# Revit family: IS_ConnectSpace_Multiproduct_BIM_DE_E0372;E0373
name_source: partatom
category: Casework
revit_build: Autodesk Revit 2015 (Build: 20140606_1530(x64)
units: mm (PartAtom-declared; Revit-internal decimal feet)

## types (8) — shared parameters
Accessories = www.idealstandard.de\ersatzteile
AreaUnits = millimeters
Assembly Code = C1030200
AssetType = Fixed
Brand = Ideal Standard
CodePerformance = FSC, EN 14749:2005
ConnectionType = Mechanical
Default Elevation = 800 mm  [stored 2.62467 ft]
Depth = 250 mm  [stored 0.82021 ft]
DurationUnit = year
ExpectedLife = 25
Height = 500 mm
IfcExportAs = IfcFurnitureType
IfcExportType = Bathroom integrated furniture
InstallationInstructions = www.idealstandard.de\produkte
LinearUnits = millimeters
ManufacturerURL = www.idealstandard.com
Material = Varies, see product information
MetalMtl = ISI_IdealStandard_Furniture_Chrome_Render
NBSDescription = Bathroom integrated furniture
NBSReference = 45-35-72/320
NominalDepth = 250 mm  [stored 0.82021 ft]
NominalHeight = 500 mm
NominalLength = 250 mm  [stored 0.82021 ft]
ProductInformation = www.idealstandard.de/produkte
Shape = Rectangular
Space = Internal
SpareParts = www.idealstandard.de/ersatzteile
Style = Bathroom cabinets
SustainabilityPerformance = FSC
URL = www.idealstandard.com
Uniclass2015Code = Pr_40_30_78_03
Uniclass2015Title = Bathroom cabinets
Uniclass2015Version = Products v1.1
Version = 2
VolumeUnits = Litres
WarrantyDurationUnit = year
zero-valued in all types: Cost

## per-type parameters (varying)
| type | BIMObjectName | BarCode | Color | Description | Features | Finish | LaminateMtl | MainColor | Model | ModelNumber | ModelReference | Name | NettWeight | NominalWidth | Size | Width |
| E0403WG - Concept Space 300 mm - Add on - Guest Unit - Gloss White | ISI_IdealStandard_BathroomIntegratedFurniture_ConnectSpace_E0403WG | 5017830455165 | Gloss White | E0373WG CONNECT SPACE side unit 300x242mm, 1 door | CONNECT SPACE side unit 300x242mm, 1 door | Gloss White | ISI_IdealStandard_Furniture_Laminate_GlossWhite_WG_Render | Gloss White | E0373WG | E0373WG | E0373WG CONNECT SPACE side unit 300x242mm, 1 door | BathroomIntegratedFurniture_ConnectSpace_E0403WG_IdealStandard | 8.75 Kg | 300 mm | 501 x 250 x 300 mm | 300 mm |
| E0403KS - Concept Space 300 mm - Add on - Guest Unit - Elm | ISI_IdealStandard_BathroomIntegratedFurniture_ConnectSpace_E0403KS | 5017830455134 | Elm | E0373KS CONNECT SPACE side unit 300x242mm, 1 door | CONNECT SPACE side unit 300x242mm, 1 door | Elm | ISI_IdealStandard_Furniture_Laminate_Elm_KS_Render | Elm | E0373KS | E0373KS | E0373KS CONNECT SPACE side unit 300x242mm, 1 door | BathroomIntegratedFurniture_ConnectSpace_E0403KS_IdealStandard | 8.75 Kg | 300 mm | 501 x 250 x 300 mm | 300 mm |
| E0403KR - Concept Space 300 mm - Add on - Guest Unit - Dark Grey | ISI_IdealStandard_BathroomIntegratedFurniture_ConnectSpace_E0403KR | 5017830455127 | Gloss Grey | E0373KR CONNECT SPACE side unit 300x242mm, 1 door | CONNECT SPACE side unit 300x242mm, 1 door | Gloss Grey | ISI_IdealStandard_Furniture_Laminate_DarkGreyKR_Render | Gloss Grey | E0373KR | E0373KR | E0373KR CONNECT SPACE side unit 300x242mm, 1 door | BathroomIntegratedFurniture_ConnectSpace_E0403KR_IdealStandard | 8.75 Kg | 300 mm | 501 x 250 x 300 mm | 300 mm |
| E0402KS - Concept Space 200 mm - Add On - Guest Unit - Elm | ISI_IdealStandard_BathroomIntegratedFurniture_ConnectSpace_E0402KS | 5017830455073 | Elm | E0372KS CONNECT SPACE side unit 200x242mm, 1 door | CONNECT SPACE side unit 200x242mm, 1 door | Elm | ISI_IdealStandard_Furniture_Laminate_Elm_KS_Render | Elm | E0372KS | E0372KS | E0372KS CONNECT SPACE side unit 200x242mm, 1 door | BathroomIntegratedFurniture_ConnectSpace_E0402KS_IdealStandard | 6.75 Kg | 200 mm | 501 x 250 x 201 mm | 200 mm |
| E0402KR - Concept Space 200 mm - Add On - Guest Unit - Gloss Grey | ISI_IdealStandard_BathroomIntegratedFurniture_ConnectSpace_E0402KR | 5017830455066 | Gloss Grey | E0372KR CONNECT SPACE side unit 200x242mm, 1 door | CONNECT SPACE side unit 200x242mm, 1 door | Gloss Grey | ISI_IdealStandard_Furniture_Laminate_DarkGreyKR_Render | Gloss Grey | E0372KR | E0372KR | E0372KR CONNECT SPACE side unit 200x242mm, 1 door | BathroomIntegratedFurniture_ConnectSpace_E0402KR_IdealStandard | 6.75 Kg | 200 mm | 501 x 250 x 201 mm | 200 mm |
| E0402WG - Concept Space 200 mm - Add On - Guest Unit - Gloss White | ISI_IdealStandard_BathroomIntegratedFurniture_ConnectSpace_E0402WG | 5017830455103 | Gloss White | E0372WG CONNECT SPACE side unit 200x242mm, 1 door | CONNECT SPACE side unit 200x242mm, 1 door | Gloss White | ISI_IdealStandard_Furniture_Laminate_GlossWhite_WG_Render | Gloss White | E0372WG | E0372WG | E0372WG CONNECT SPACE side unit 200x242mm, 1 door | BathroomIntegratedFurniture_ConnectSpace_E0402WG_IdealStandard | 6.75 Kg | 200 mm | 501 x 250 x 201 mm | 200 mm |
| E0403SO - Concept Space 300 mm - Add on - Guest Unit - American Oak | ISI_IdealStandard_BathroomIntegratedFurniture_ConnectSpace_E0403SO | 5017830455141 | American Oak | E0373SO CONNECT SPACE side unit 300x242mm, 1 door | CONNECT SPACE side unit 300x242mm, 1 door | American Oak | ISI_IdealStandard_Furniture_Laminate_AmericanOak_SO_Render | American Oak | E0373SO | E0373SO | E0373SO CONNECT SPACE side unit 300x242mm, 1 door | BathroomIntegratedFurniture_ConnectSpace_E0403SO_IdealStandard | 8.75 Kg | 300 mm | 501 x 250 x 300 mm | 300 mm |
| E0402SO - Concept Space 200 mm - Add On - Guest Unit - American Oak | ISI_IdealStandard_BathroomIntegratedFurniture_ConnectSpace_E0402SO | 5017830451020 | American Oak | E0372SO CONNECT SPACE side unit 200x242mm, 1 door | CONNECT SPACE side unit 200x242mm, 1 door | American Oak | ISI_IdealStandard_Furniture_Laminate_AmericanOak_SO_Render | American Oak | E0372SO | E0372SO | E0372SO CONNECT SPACE side unit 200x242mm, 1 door | BathroomIntegratedFurniture_ConnectSpace_E0402SO_IdealStandard | 6.75 Kg | 200 mm | 501 x 250 x 201 mm | 200 mm |

note: [stored X ft] marks values corroborated as IEEE doubles in the binary element streams (Revit-internal decimal feet)

## geometry (parser evidence)
native form markers: Blend x2, Sweep x3
no freeform markers — native parametric forms only
